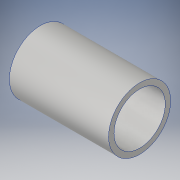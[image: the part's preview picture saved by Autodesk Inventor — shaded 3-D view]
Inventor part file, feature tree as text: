
AUTODESK INVENTOR PART (.ipt)
format: ipt  version: 2019 (Build 230136000, 136)  size: 108,544 bytes
history: native  units: mm
features: sketch x2, revolve x1, extrude x1
ambient origin geometry x8: Origin, YZ Plane, XZ Plane, XY Plane, X Axis, Y Axis, Z Axis, Center Point
bodies: Solid1 (feature_tree)
feature tree (4):
  revolve  "Revolution1"  [1 undecoded]
  extrude  "Extrusion1"  Depth=58.125mm
  sketch  "Sketch1"  dims[d0=75.0mm d1=120.0mm]
  sketch  "Sketch2"  dims[d2=75.0mm d3=58.125mm d4=90.0deg d5=6.5mm d6=100.0mm d7=0.0mm]
note: 1 required parameter value undecoded (feature->parameter linkage not recoverable at this tier; creation-order binding heuristic only, values carry confidence <= 0.55)
